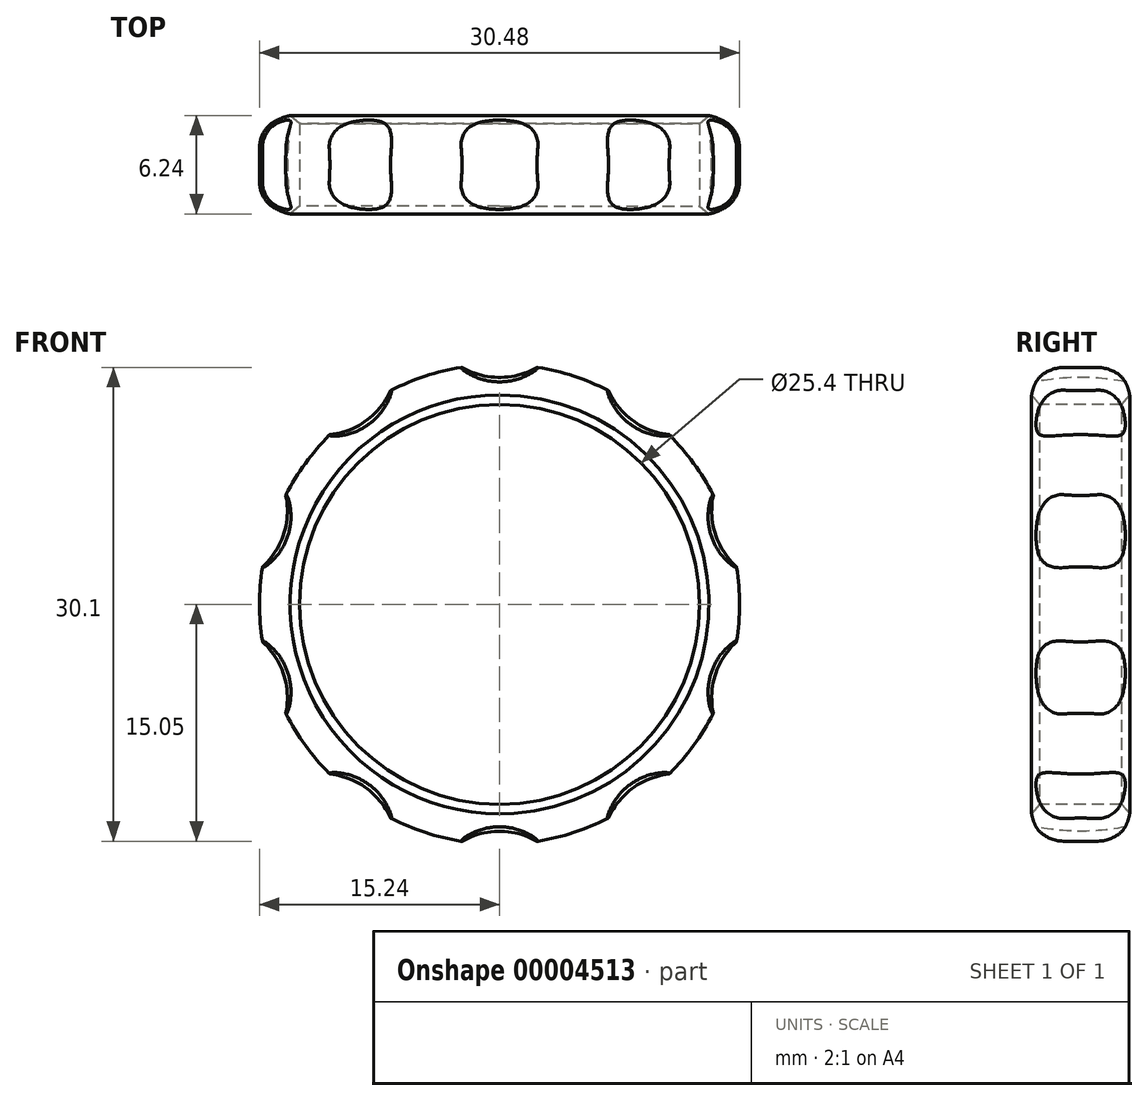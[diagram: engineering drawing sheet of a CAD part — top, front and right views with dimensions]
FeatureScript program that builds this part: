
annotation { "Feature Type Name" : "Feature", "Feature Type Description" : "" }
export const myFeature = defineFeature(function(context is Context, id is Id, definition is map)
    precondition{}
    {
        {
            var Q0;
            Q0=qCreatedBy(makeId("Right.planeOp"),FACE);
            var sketch = newSketch(context, id + "F0", { "sketchPlane" : qUnion([Q0])});
            skLineSegment(sketch, "E0", {"start": v(0, 0) * mm, "end": v(0, 12.7) * mm, "construction": true});
            skLineSegment(sketch, "E1", {"start": v(-3.17, 12.7) * mm, "end": v(3.18, 12.7) * mm});
            skArc(sketch, "E2", {"start": v(3.18, 12.7) * mm, "mid": v(0, 15.88) * mm, "end": v(-3.18, 12.7) * mm});
            skLineSegment(sketch, "E3", {"start": v(0, 0) * mm, "end": v(4.07, 0) * mm, "construction": true});
            skLineSegment(sketch, "E4", {"start": v(-1.9, 15.24) * mm, "end": v(1.9, 15.24) * mm});
            skSolve(sketch);
        }
        {
            var Q0;
            Q0=makeQuery(id+"F0.imprint","IMPRINT",FACE,{"disambiguationData":[TD([[makeQuery(id+"F0.imprint","IMPRINT",EDGE,{"derivedFrom":sQuery(id+"F0.wireOp",EDGE,"E1")}),1.0]])]});
            var Q1;
            Q1=sQuery(id+"F0.wireOp",EDGE,"E3");
            revolve(context, id + "F1", {"entities" : qUnion([Q0]), "axis" : qUnion([Q1]), "revolveType" : RevolveType.FULL});
        }
        {
            var Q0;
            {var subQ0=sQuery(id+"F0.wireOp",EDGE,"E1");var subQ1=sQuery(id+"F0.wireOp",EDGE,"E2");Q0=makeQuery(id+"F1.opRevolve","SWEPT_EDGE",EDGE,{"disambiguationData":[OSD([subQ0,subQ1]),TDD([makeQuery(id+"F0.imprint","INTERSECT",VERTEX,{"disambiguationData":[OD(0.0)],"derivedFrom":[subQ0,subQ1]})])]});}
            var Q1;
            {var subQ0=sQuery(id+"F0.wireOp",EDGE,"E1");var subQ1=sQuery(id+"F0.wireOp",EDGE,"E2");Q1=makeQuery(id+"F1.opRevolve","SWEPT_EDGE",EDGE,{"disambiguationData":[OSD([subQ0,subQ1]),TDD([makeQuery(id+"F0.imprint","INTERSECT",VERTEX,{"disambiguationData":[OD(1.0)],"derivedFrom":[subQ0,subQ1]})])]});}
            chamfer(context, id + "F2", {"entities" : qUnion([Q0, Q1]), "width" : 0.5 * mm, "tangentPropagation" : true});
        }
        {
            var Q0;
            Q0=qCreatedBy(makeId("Front.planeOp"),FACE);
            var sketch = newSketch(context, id + "F3", { "sketchPlane" : qUnion([Q0])});
            skLineSegment(sketch, "E5", {"start": v(0, 0) * mm, "end": v(22.28, 0) * mm, "construction": true});
            skLineSegment(sketch, "E6", {"start": v(0, 0) * mm, "end": v(0, 19.18) * mm, "construction": true});
            skLineSegment(sketch, "E7", {"start": v(0, 9.59) * mm, "end": v(22.28, 9.59) * mm, "construction": true});
            skCircle(sketch, "E8", {"center": v(0, 19.18) * mm, "radius": 4.76 * mm});
            skSolve(sketch);
        }
        {
            var Q0;
            {var subQ0=sQuery(id+"F0.wireOp",EDGE,"E2");var subQ1=sQuery(id+"F0.wireOp",EDGE,"E4");Q0=makeQuery(id+"F1.opRevolve","SWEPT_EDGE",EDGE,{"disambiguationData":[OSD([subQ0,subQ1]),TDD([makeQuery(id+"F0.imprint","INTERSECT",VERTEX,{"disambiguationData":[OD(0.0)],"derivedFrom":[subQ0,subQ1]})])]});}
            var Q1;
            {var subQ0=sQuery(id+"F0.wireOp",EDGE,"E2");var subQ1=sQuery(id+"F0.wireOp",EDGE,"E4");Q1=makeQuery(id+"F1.opRevolve","SWEPT_EDGE",EDGE,{"disambiguationData":[OSD([subQ0,subQ1]),TDD([makeQuery(id+"F0.imprint","INTERSECT",VERTEX,{"disambiguationData":[OD(1.0)],"derivedFrom":[subQ0,subQ1]})])]});}
            fillet(context, id + "F4", {"entities" : qUnion([Q0, Q1]), "radius" : 1.9 * mm, "tangentPropagation" : true, "allowEdgeOverflow" : false});
        }
        {
            var Q0;
            Q0=makeQuery(id+"F3.imprint","IMPRINT",FACE,{"disambiguationData":[TD([[makeQuery(id+"F3.imprint","IMPRINT",EDGE,{"derivedFrom":sQuery(id+"F3.wireOp",EDGE,"E8")}),1.0]])]});
            var Q1;
            Q1=sQuery(id+"F3.wireOp",EDGE,"E5");
            revolve(context, id + "F5", {"operationType" : NewBodyOperationType.REMOVE, "entities" : qUnion([Q0]), "axis" : qUnion([Q1]), "revolveType" : RevolveType.FULL, "oppositeDirection" : true});
        }
        {
            var Q0;
            Q0=makeQuery(id+"F5.boolean.opBoolean","COPY",FACE,{"disambiguationData":[OD(1.0)],"derivedFrom":makeQuery(id+"F5.opRevolve","SWEPT_FACE",FACE,{"disambiguationData":[OSD([sQuery(id+"F3.wireOp",EDGE,"E8")])]})});
            var Q1;
            Q1=makeQuery(id+"F5.boolean.opBoolean","COPY",FACE,{"disambiguationData":[OD(0.0)],"derivedFrom":makeQuery(id+"F5.opRevolve","SWEPT_FACE",FACE,{"disambiguationData":[OSD([sQuery(id+"F3.wireOp",EDGE,"E8")])]})});
            var Q2;
            Q2=makeQuery(id+"F1.opRevolve","SWEPT_BODY",BODY,{"disambiguationData":[OSD([sQuery(id+"F0.wireOp",EDGE,"E1"),sQuery(id+"F0.wireOp",EDGE,"E2")])]});
            var Q3;
            {var subQ0=sQuery(id+"F0.wireOp",EDGE,"E1");var subQ1=sQuery(id+"F0.wireOp",EDGE,"E2");Q3=makeQuery(id+"F2.opChamfer","BLEND_EDGE",EDGE,{"blendedFrom":[makeQuery(id+"F1.opRevolve","SWEPT_EDGE",EDGE,{"disambiguationData":[OSD([subQ0,subQ1]),TDD([makeQuery(id+"F0.imprint","INTERSECT",VERTEX,{"disambiguationData":[OD(1.0)],"derivedFrom":[subQ0,subQ1]})])]}),makeQuery(id+"F1.opRevolve","SWEPT_FACE",FACE,{"disambiguationData":[OSD([subQ0])]})],"blendedInto":[makeQuery(id+"F1.opRevolve","SWEPT_FACE",FACE,{"disambiguationData":[OSD([subQ0])]})]});}
            circularPattern(context, id + "F6", {"faces" : qUnion([Q0, Q1]), "axis" : qUnion([Q3]), "angle" : 180 / 5 * degree, "instanceCount" : 5, "patternType" : PatternType.FACE});
        }
    });
